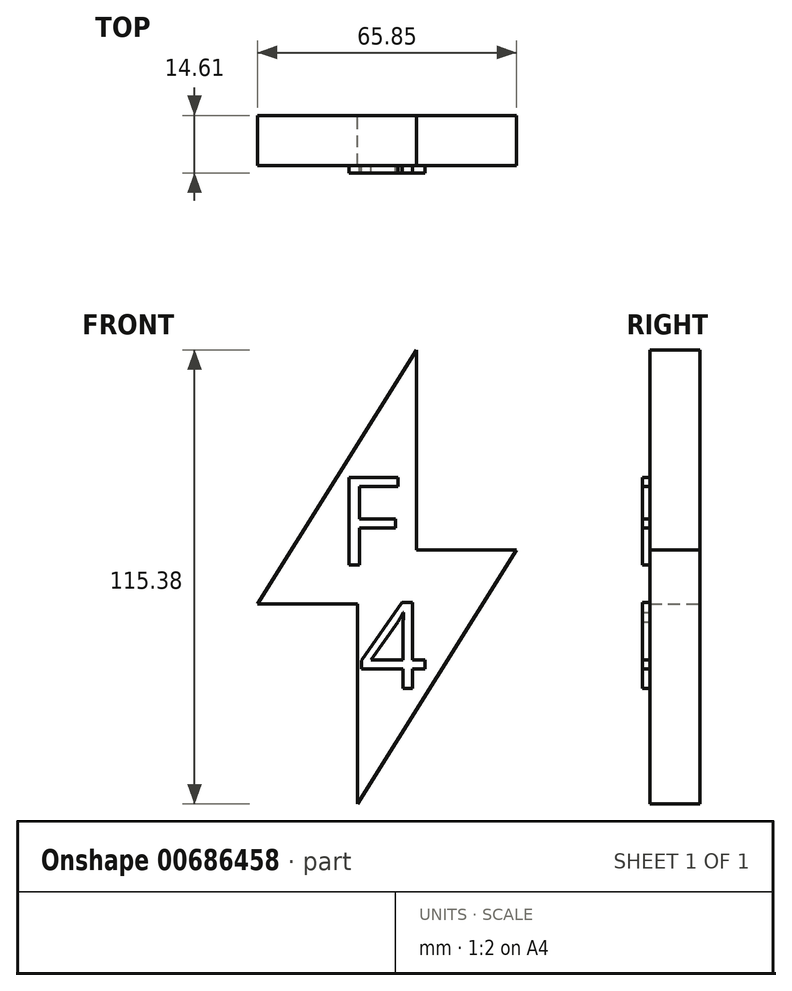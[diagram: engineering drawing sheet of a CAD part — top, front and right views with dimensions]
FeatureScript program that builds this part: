
annotation { "Feature Type Name" : "Feature", "Feature Type Description" : "" }
export const myFeature = defineFeature(function(context is Context, id is Id, definition is map)
    precondition{}
    {
        {
            var Q0;
            Q0=qCreatedBy(makeId("Front.planeOp"),FACE);
            var sketch = newSketch(context, id + "F0", { "sketchPlane" : qUnion([Q0])});
            skLineSegment(sketch, "E0", {"start": v(29.97, 45.38) * mm, "end": v(29.97, -5.42) * mm});
            skLineSegment(sketch, "E1", {"start": v(29.97, -5.42) * mm, "end": v(55.37, -5.42) * mm});
            skLineSegment(sketch, "E2", {"start": v(55.37, -5.42) * mm, "end": v(14.92, -70) * mm});
            skLineSegment(sketch, "E3", {"start": v(14.92, -70) * mm, "end": v(14.92, -19.2) * mm});
            skLineSegment(sketch, "E4", {"start": v(14.92, -19.2) * mm, "end": v(-10.48, -19.2) * mm});
            skLineSegment(sketch, "E5", {"start": v(-10.48, -19.2) * mm, "end": v(29.97, 45.38) * mm});
            skSolve(sketch);
        }
        {
            var Q0;
            Q0=makeQuery(id+"F0.imprint","IMPRINT",FACE,{"disambiguationData":[TD([[makeQuery(id+"F0.imprint","IMPRINT",EDGE,{"derivedFrom":sQuery(id+"F0.wireOp",EDGE,"E0")}),-1.0]])]});
            extrude(context, id + "F1", {"entities" : qUnion([Q0]), "depth" : 12.7 * mm, "offsetDistance" : 25.4 * mm});
        }
        {
            var Q0;
            Q0=makeQuery(id+"F1.opExtrude","CAP_FACE",FACE,{"disambiguationData":[OSD([sQuery(id+"F0.wireOp",EDGE,"E0"),sQuery(id+"F0.wireOp",EDGE,"E1"),sQuery(id+"F0.wireOp",EDGE,"E2"),sQuery(id+"F0.wireOp",EDGE,"E3"),sQuery(id+"F0.wireOp",EDGE,"E4"),sQuery(id+"F0.wireOp",EDGE,"E5")])],"isStart":false});
            var sketch = newSketch(context, id + "F2", { "sketchPlane" : qUnion([Q0])});
            skText(sketch, "E6", { "text": "F\n\n", "fontName": "OpenSans-Regular.ttf"});
            const initialGuessF2  = {"E6": [0.00977, -0.00929, 1, 0, 0.02242]};
            skSetInitialGuess(sketch, initialGuessF2);
            skSolve(sketch);
        }
        {
            var Q0;
            Q0=makeQuery(id+"F2.imprint","IMPRINT",FACE,{"disambiguationData":[TD([[makeQuery(id+"F2.imprint","IMPRINT",EDGE,{"derivedFrom":sQuery(id+"F2.wireOp",EDGE,"E6.sketch_text.stroke-0")}),1.0]])]});
            var sketch = newSketch(context, id + "F3", { "sketchPlane" : qUnion([Q0])});
            skText(sketch, "E7", { "text": "4\n", "fontName": "OpenSans-Regular.ttf"});
            const initialGuessF3  = {"E7": [0.0153, -0.0406, 1, 0, 0.02193]};
            skSetInitialGuess(sketch, initialGuessF3);
            skSolve(sketch);
        }
        {
            var Q0;
            Q0 = qSketchRegion(id + "F2", true);
            extrude(context, id + "F4", {"entities" : qUnion([Q0]), "operationType" : NewBodyOperationType.ADD, "depth" : 1.9 * mm, "offsetDistance" : 25.4 * mm});
        }
        {
            var Q0;
            Q0 = qSketchRegion(id + "F3", true);
            extrude(context, id + "F5", {"entities" : qUnion([Q0]), "operationType" : NewBodyOperationType.ADD, "depth" : 1.9 * mm, "offsetDistance" : 25.4 * mm});
        }
    });
